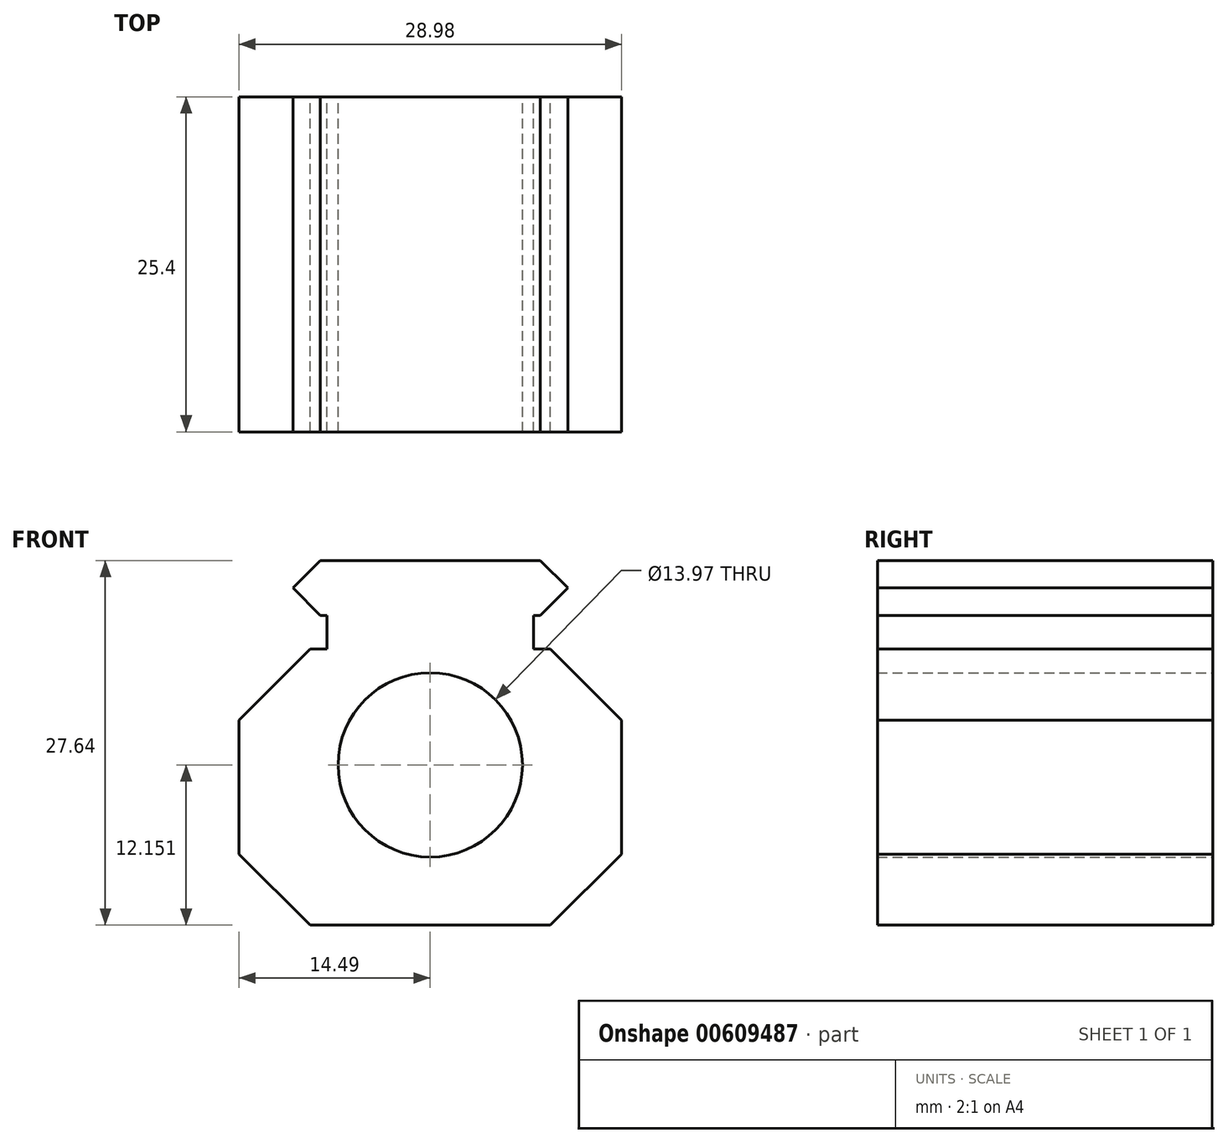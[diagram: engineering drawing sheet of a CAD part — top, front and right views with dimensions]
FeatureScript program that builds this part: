
annotation { "Feature Type Name" : "Feature", "Feature Type Description" : "" }
export const myFeature = defineFeature(function(context is Context, id is Id, definition is map)
    precondition{}
    {
        {
            var Q0;
            Q0=qCreatedBy(makeId("Front.planeOp"),FACE);
            var sketch = newSketch(context, id + "F0", { "sketchPlane" : qUnion([Q0])});
            skLineSegment(sketch, "E0", {"start": v(0, 19.11) * mm, "end": v(10.62, 19.11) * mm});
            skLineSegment(sketch, "E1", {"start": v(10.62, 19.11) * mm, "end": v(10.62, 14.94) * mm});
            skLineSegment(sketch, "E2", {"start": v(10.62, 14.94) * mm, "end": v(7.84, 14.94) * mm});
            skLineSegment(sketch, "E3", {"start": v(7.84, 14.94) * mm, "end": v(7.84, 12.4) * mm});
            skLineSegment(sketch, "E4", {"start": v(7.84, 12.4) * mm, "end": v(9.1, 12.4) * mm});
            skLineSegment(sketch, "E5", {"start": v(9.1, 12.4) * mm, "end": v(14.5, 7.02) * mm});
            skLineSegment(sketch, "E6", {"start": v(14.5, 7.02) * mm, "end": v(14.5, -3.14) * mm});
            skLineSegment(sketch, "E7", {"start": v(14.5, -3.14) * mm, "end": v(9.1, -8.53) * mm});
            skLineSegment(sketch, "E8", {"start": v(9.1, -8.53) * mm, "end": v(0, -8.53) * mm});
            skLineSegment(sketch, "E9", {"start": v(0, -8.53) * mm, "end": v(0, 19.11) * mm});
            skLineSegment(sketch, "E10.MirrorCS", {"start": v(0, 19.11) * mm, "end": v(-10.62, 19.11) * mm});
            skLineSegment(sketch, "E11.MirrorCS", {"start": v(-10.62, 19.11) * mm, "end": v(-10.62, 14.94) * mm});
            skLineSegment(sketch, "E12.MirrorCS", {"start": v(-10.62, 14.94) * mm, "end": v(-7.84, 14.94) * mm});
            skLineSegment(sketch, "E13.MirrorCS", {"start": v(-7.84, 14.94) * mm, "end": v(-7.84, 12.4) * mm});
            skLineSegment(sketch, "E14.MirrorCS", {"start": v(-7.84, 12.4) * mm, "end": v(-9.1, 12.4) * mm});
            skLineSegment(sketch, "E15.MirrorCS", {"start": v(-9.1, 12.4) * mm, "end": v(-14.5, 7.02) * mm});
            skLineSegment(sketch, "E16.MirrorCS", {"start": v(-14.5, 7.02) * mm, "end": v(-14.5, -3.14) * mm});
            skLineSegment(sketch, "E17.MirrorCS", {"start": v(-14.5, -3.14) * mm, "end": v(-9.1, -8.53) * mm});
            skLineSegment(sketch, "E18.MirrorCS", {"start": v(-9.1, -8.53) * mm, "end": v(0, -8.53) * mm});
            skSolve(sketch);
        }
        {
            var Q0;
            Q0=makeQuery(id+"F0.imprint","IMPRINT",FACE,{"disambiguationData":[TD([[makeQuery(id+"F0.imprint","IMPRINT",EDGE,{"derivedFrom":sQuery(id+"F0.wireOp",EDGE,"E0")}),-1.0]])]});
            var Q1;
            Q1=makeQuery(id+"F0.imprint","IMPRINT",FACE,{"disambiguationData":[TD([[makeQuery(id+"F0.imprint","IMPRINT",EDGE,{"derivedFrom":sQuery(id+"F0.wireOp",EDGE,"E9")}),1.0]])]});
            extrude(context, id + "F1", {"entities" : qUnion([Q0, Q1]), "depth" : 25.4 * mm, "offsetDistance" : 25.4 * mm});
        }
        {
            var Q0;
            Q0=makeQuery(id+"F1.opExtrude","CAP_FACE",FACE,{"disambiguationData":[OSD([sQuery(id+"F0.wireOp",EDGE,"E0"),sQuery(id+"F0.wireOp",EDGE,"E1"),sQuery(id+"F0.wireOp",EDGE,"E2"),sQuery(id+"F0.wireOp",EDGE,"E3"),sQuery(id+"F0.wireOp",EDGE,"E4"),sQuery(id+"F0.wireOp",EDGE,"E5"),sQuery(id+"F0.wireOp",EDGE,"E6"),sQuery(id+"F0.wireOp",EDGE,"E7"),sQuery(id+"F0.wireOp",EDGE,"E8"),sQuery(id+"F0.wireOp",EDGE,"E10.MirrorCS"),sQuery(id+"F0.wireOp",EDGE,"E11.MirrorCS"),sQuery(id+"F0.wireOp",EDGE,"E12.MirrorCS"),sQuery(id+"F0.wireOp",EDGE,"E13.MirrorCS"),sQuery(id+"F0.wireOp",EDGE,"E14.MirrorCS"),sQuery(id+"F0.wireOp",EDGE,"E15.MirrorCS"),sQuery(id+"F0.wireOp",EDGE,"E16.MirrorCS"),sQuery(id+"F0.wireOp",EDGE,"E17.MirrorCS"),sQuery(id+"F0.wireOp",EDGE,"E18.MirrorCS")])],"isStart":true});
            var sketch = newSketch(context, id + "F2", { "sketchPlane" : qUnion([Q0])});
            skPoint(sketch, "E19", {"position": v(0, 3.62) * mm});
            skSolve(sketch);
        }
        {
            var Q0;
            Q0=sQuery(id+"F2.wireOp",VERTEX,"E19");
            var Q1;
            Q1=makeQuery(id+"F1.opExtrude","SWEPT_BODY",BODY,{"disambiguationData":[OSD([sQuery(id+"F0.wireOp",EDGE,"E0"),sQuery(id+"F0.wireOp",EDGE,"E1"),sQuery(id+"F0.wireOp",EDGE,"E2"),sQuery(id+"F0.wireOp",EDGE,"E3"),sQuery(id+"F0.wireOp",EDGE,"E4"),sQuery(id+"F0.wireOp",EDGE,"E5"),sQuery(id+"F0.wireOp",EDGE,"E6"),sQuery(id+"F0.wireOp",EDGE,"E7"),sQuery(id+"F0.wireOp",EDGE,"E8"),sQuery(id+"F0.wireOp",EDGE,"E10.MirrorCS"),sQuery(id+"F0.wireOp",EDGE,"E11.MirrorCS"),sQuery(id+"F0.wireOp",EDGE,"E12.MirrorCS"),sQuery(id+"F0.wireOp",EDGE,"E13.MirrorCS"),sQuery(id+"F0.wireOp",EDGE,"E14.MirrorCS"),sQuery(id+"F0.wireOp",EDGE,"E15.MirrorCS"),sQuery(id+"F0.wireOp",EDGE,"E16.MirrorCS"),sQuery(id+"F0.wireOp",EDGE,"E17.MirrorCS"),sQuery(id+"F0.wireOp",EDGE,"E18.MirrorCS")])]});
            hole(context, id + "F3", {"style" : HoleStyle.SIMPLE, "endStyle" : HoleEndStyle.BLIND, "holeDiameter" : 13.97 * mm, "majorDiameter" : 6.35 * mm, "holeDepth" : 25.4 * mm, "isTappedThrough" : true, "tappedDepth" : 12.7 * mm, "tapClearance" : 3, "startFromSketch" : true, "locations" : qUnion([Q0]), "scope" : qUnion([Q1])});
        }
        {
            var Q0;
            Q0=makeQuery(id+"F1.opExtrude","SWEPT_EDGE",EDGE,{"disambiguationData":[OSD([sQuery(id+"F0.wireOp",EDGE,"E1"),sQuery(id+"F0.wireOp",EDGE,"E2")])]});
            var Q1;
            Q1=makeQuery(id+"F1.opExtrude","SWEPT_EDGE",EDGE,{"disambiguationData":[OSD([sQuery(id+"F0.wireOp",EDGE,"E0"),sQuery(id+"F0.wireOp",EDGE,"E1")])]});
            var Q2;
            Q2=makeQuery(id+"F1.opExtrude","SWEPT_EDGE",EDGE,{"disambiguationData":[OSD([sQuery(id+"F0.wireOp",EDGE,"E10.MirrorCS"),sQuery(id+"F0.wireOp",EDGE,"E11.MirrorCS")])]});
            var Q3;
            Q3=makeQuery(id+"F1.opExtrude","SWEPT_EDGE",EDGE,{"disambiguationData":[OSD([sQuery(id+"F0.wireOp",EDGE,"E11.MirrorCS"),sQuery(id+"F0.wireOp",EDGE,"E12.MirrorCS")])]});
            chamfer(context, id + "F4", {"entities" : qUnion([Q0, Q1, Q2, Q3]), "width" : 2.3 * mm, "tangentPropagation" : true});
        }
    });
